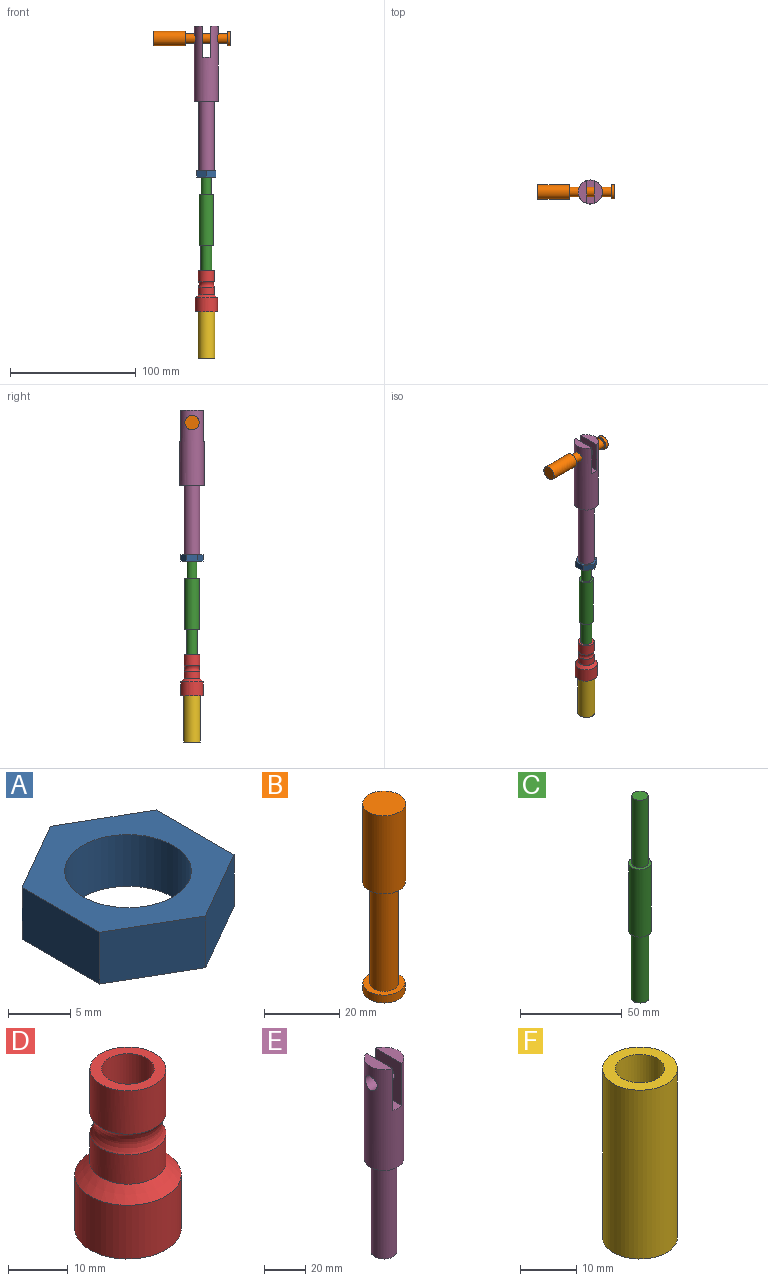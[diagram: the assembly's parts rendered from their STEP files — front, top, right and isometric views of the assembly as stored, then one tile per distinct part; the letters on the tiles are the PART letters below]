
ASSEMBLY  parts=6 mates=5
PART A: 9 faces, bbox 15.2x17.6x5.1 mm
  f0: plane 7.62x5.08mm, normal (0.5,-0.87,0), area 44.7mm2, adj f1,f6,f7,f8
  f1: plane 8.8x5.08mm, normal (1,0,0), area 44.7mm2, adj f0,f2,f7,f8
  f2: plane 7.62x5.08mm, normal (0.5,0.87,0), area 44.7mm2, adj f1,f3,f7,f8
  f3: plane 7.62x5.08mm, normal (-0.5,0.87,0), area 44.7mm2, adj f2,f4,f7,f8
  f4: plane 8.8x5.08mm, normal (-1,0,0), area 44.7mm2, adj f3,f6,f7,f8
  f5: cylinder r=5.08mm len=10.16mm, axis (0,0,-1), area 162.1mm2, adj f7,f8
  f6: plane 7.62x5.08mm, normal (-0.5,-0.87,0), area 44.7mm2, adj f0,f4,f7,f8
  f7: plane 17.6x15.24mm, normal (0,0,1), area 120.1mm2, adj f0,f1,f2,f3,f4,f5,f6
  f8: plane 17.6x15.24mm, normal (0,0,-1), area 120.1mm2, adj f0,f1,f2,f3,f4,f5,f6
PART B: 7 faces, bbox 11.4x11.4x61 mm
  f0: cylinder r=3.81mm len=33.02mm, axis (0,0,-1), area 790.5mm2, adj f2,f5
  f1: cylinder r=5.59mm len=11.18mm, axis (0,0,-1), area 89.2mm2, adj f2,f3
  f2: plane 11.18x11.18mm, normal (0,0,1), area 52.5mm2, adj f0,f1
  f3: plane 11.18x11.18mm, normal (0,0,-1), area 98.1mm2, adj f1
  f4: cylinder r=5.71mm len=25.4mm, axis (0,0,1), area 912.1mm2, adj f5,f6
  f5: plane 11.43x11.43mm, normal (0,0,-1), area 57mm2, adj f0,f4
  f6: plane 11.43x11.43mm, normal (0,0,1), area 102.6mm2, adj f4
PART C: 7 faces, bbox 11.3x11.3x121.9 mm
  f0: cylinder r=4.39mm len=40.64mm, axis (0,0,-1), area 1122.1mm2, adj f3,f6
  f1: cylinder r=5.65mm len=40.64mm, axis (0,0,-1), area 1442.5mm2, adj f2,f3
  f2: plane 11.3x11.3mm, normal (0,0,1), area 50.8mm2, adj f1,f4
  f3: plane 11.3x11.3mm, normal (0,0,-1), area 39.6mm2, adj f0,f1
  f4: cylinder r=3.97mm len=40.64mm, axis (0,0,-1), area 1013.4mm2, adj f2,f5
  f5: plane 7.94x7.94mm, normal (0,0,1), area 49.5mm2, adj f4
  f6: plane 8.79x8.79mm, normal (0,0,-1), area 60.7mm2, adj f0
PART D: 8 faces, bbox 17.8x17.8x32.6 mm
  f0: cylinder r=8.89mm len=17.78mm, axis (0,0,1), area 612.9mm2, adj f2,f7
  f1: plane 12.7x12.7mm, normal (0,0,1), area 66.1mm2, adj f3,f5
  f2: plane 17.78x17.78mm, normal (0,0,-1), area 187.7mm2, adj f0,f3
  f3: cylinder r=4.39mm len=32.56mm, axis (0,0,1), area 898.2mm2, adj f1,f2
  f4: cylinder r=6.35mm len=12.7mm, axis (0,0,1), area 238.5mm2, adj f6,f7
  f5: cylinder r=6.35mm len=12.7mm, axis (0,0,1), area 353.5mm2, adj f1,f6
  f6: torus R=9.53mm, axis (0,0,1), area 166.3mm2, adj f4,f5
  f7: cone r=6.35mm half-angle=45deg, axis (0,0,-1), area 172mm2, adj f0,f4
PART E: 13 faces, bbox 19.1x19.1x115 mm
  f0: cylinder r=9.55mm len=60mm, axis (0,0,-1), area 3187mm2, adj f1,f2,f5,f6,f7,f8,f9,f10
  f1: plane 18.13x6.55mm, normal (0,0,1), area 86.9mm2, adj f0,f9
  f2: cylinder r=4.1mm len=8.2mm, axis (-1,0,0), area 157mm2, adj f0,f9
  f3: cylinder r=6.25mm len=55mm, axis (0,0,-1), area 2159.8mm2, adj f4,f6
  f4: plane 12.5x12.5mm, normal (0,0,-1), area 73.2mm2, adj f3,f11
  f5: plane 18.13x6.55mm, normal (0,0,1), area 86.9mm2, adj f0,f10
  f6: plane 19.1x19.1mm, normal (0,0,-1), area 163.8mm2, adj f0,f3
  f7: cylinder r=4.1mm len=8.2mm, axis (-1,0,0), area 157mm2, adj f0,f10
  f8: plane 19.1x6mm, normal (0,0,1), area 112.7mm2, adj f0,f9,f10
  f9: plane 25x18.13mm, normal (-1,0,0), area 400.5mm2, adj f0,f1,f2,f8
  f10: plane 25x18.13mm, normal (1,0,0), area 400.5mm2, adj f0,f5,f7,f8
  f11: cylinder r=3.97mm len=22mm, axis (0,0,-1), area 548.6mm2, adj f4,f12
  f12: plane 7.94x7.94mm, normal (0,0,-1), area 49.5mm2, adj f11
PART F: 4 faces, bbox 13.3x13.3x36.8 mm
  f0: cylinder r=6.67mm len=36.83mm, axis (0,0,1), area 1542.9mm2, adj f1,f2
  f1: plane 13.34x13.34mm, normal (0,0,-1), area 79.1mm2, adj f0,f3
  f2: plane 13.34x13.34mm, normal (0,0,1), area 79.1mm2, adj f0,f3
  f3: cylinder r=4.39mm len=36.83mm, axis (0,0,1), area 1015.9mm2, adj f1,f2
PLACE A t=(0,10.79,-55.45)mm
PLACE B rot(axis=(-0.58,-0.58,0.58),120deg) t=(19.05,10.79,54.63)mm
PLACE C t=(0,10.79,-129.97)mm
PLACE D rot(axis=(0,0,-1),31.3deg) t=(0,10.79,-137.13)mm
PLACE E t=(0,10.79,-50.37)mm
PLACE F rot(axis=(0,0,-1),31.3deg) t=(0,10.79,-137.13)mm
MATE revolute B.f0 <-> E.f2  axis (1,0,0) through (0,10.79,54.63)mm
MATE revolute C.f0 <-> D.f4  axis (0,0,-1) through (0,10.79,-129.97)mm
MATE revolute F.f0 <-> D.f0  axis (0,0,1) through (0,10.79,-162.53)mm
MATE revolute C.f4 <-> E.f11  axis (0,0,-1) through (0,10.79,-28.37)mm
MATE revolute A.f5 <-> E.f0  axis (0,0,1) through (0,10.79,-50.37)mm
